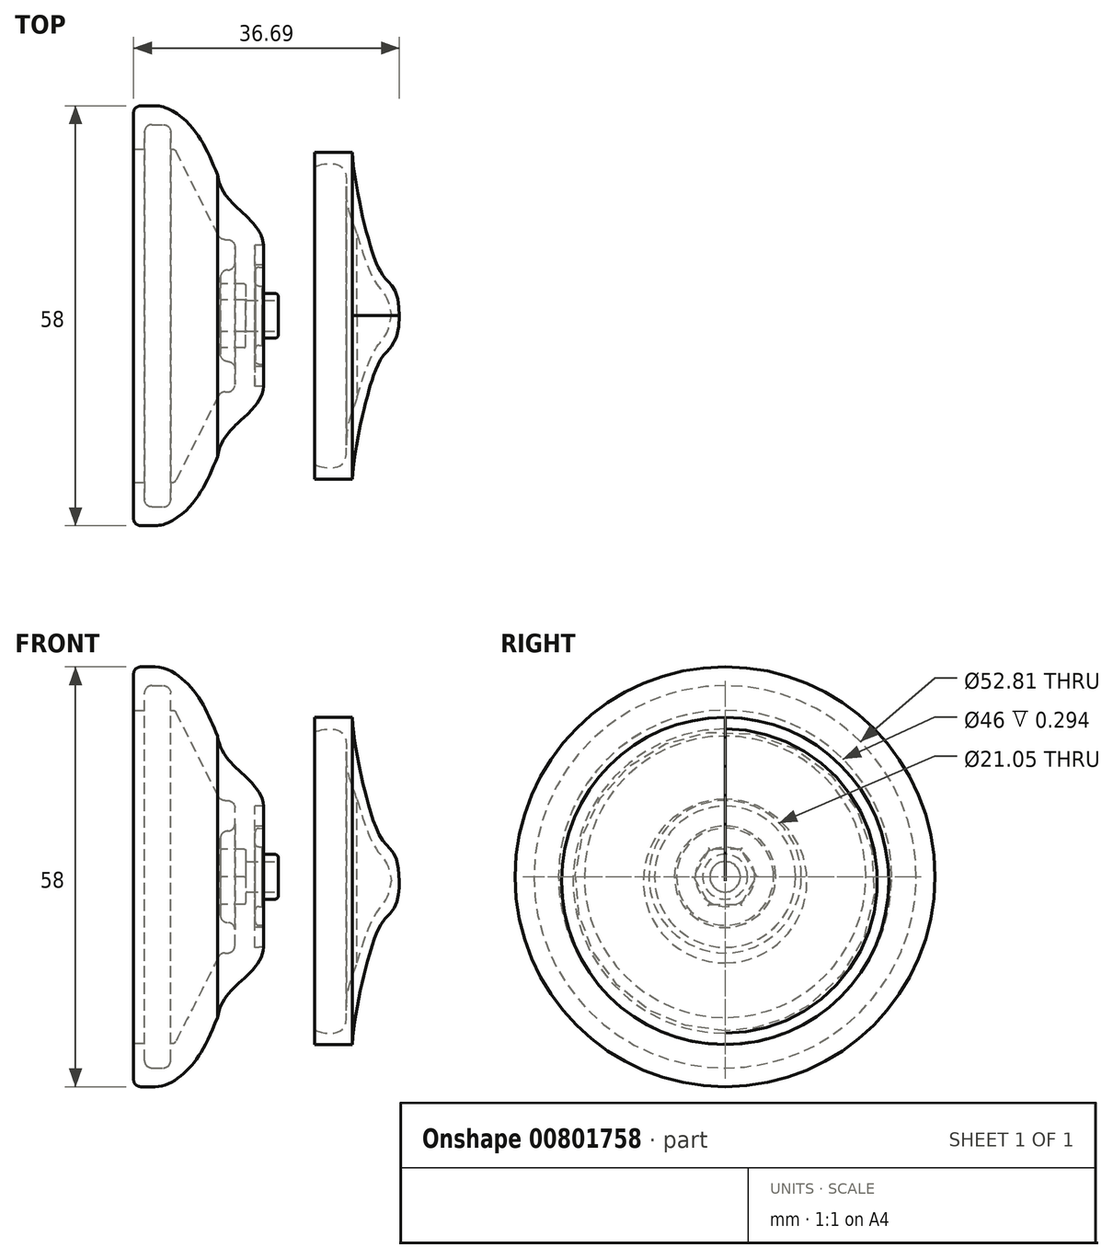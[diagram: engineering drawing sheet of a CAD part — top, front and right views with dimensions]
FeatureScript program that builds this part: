
annotation { "Feature Type Name" : "Feature", "Feature Type Description" : "" }
export const myFeature = defineFeature(function(context is Context, id is Id, definition is map)
    precondition{}
    {
        {
            var Q0;
            Q0=qCreatedBy(makeId("Front.planeOp"),FACE);
            var sketch = newSketch(context, id + "F0", { "sketchPlane" : qUnion([Q0])});
            skPoint(sketch, "E0", {"position": v(36.58, 0) * mm});
            skLineSegment(sketch, "E1", {"start": v(40.53, -3.33) * mm, "end": v(40.53, -2.83) * mm});
            skLineSegment(sketch, "E2", {"start": v(40.03, -2.33) * mm, "end": v(38.28, -2.33) * mm});
            skLineSegment(sketch, "E3", {"start": v(38.28, -2.33) * mm, "end": v(38.28, -1.33) * mm});
            skLineSegment(sketch, "E4", {"start": v(38.28, -1.33) * mm, "end": v(37.83, -1.33) * mm});
            skLineSegment(sketch, "E5", {"start": v(37.33, -0.83) * mm, "end": v(37.33, 0.76) * mm});
            skLineSegment(sketch, "E6", {"start": v(37.82, 1.26) * mm, "end": v(38.46, 1.27) * mm});
            skLineSegment(sketch, "E7", {"start": v(38.46, 1.27) * mm, "end": v(38.46, 1.57) * mm});
            skLineSegment(sketch, "E8", {"start": v(38.46, 1.57) * mm, "end": v(37.26, 1.57) * mm});
            skLineSegment(sketch, "E9", {"start": v(37.26, 1.57) * mm, "end": v(37.26, 4.32) * mm});
            skLineSegment(sketch, "E10", {"start": v(37.26, 4.32) * mm, "end": v(38.46, 4.32) * mm});
            skPoint(sketch, "E11.startSnap0", {"position": v(39.4, -2.33) * mm});
            skLineSegment(sketch, "E12", {"start": v(36.03, -3.33) * mm, "end": v(40.53, -3.33) * mm});
            skLineSegment(sketch, "E13", {"start": v(40.53, -5.43) * mm, "end": v(38.22, -5.43) * mm});
            skLineSegment(sketch, "E14", {"start": v(40.53, -5.43) * mm, "end": v(20.53, -5.43) * mm});
            skLineSegment(sketch, "E15", {"start": v(21.52, 23.57) * mm, "end": v(23.51, 23.57) * mm});
            skFitSpline(sketch, "E16", {"points": [v(23.51, 23.57) * mm, v(27.76, 21.46) * mm, v(32.12, 14) * mm], "startDerivative": vector(10.57, 0) * mm, "endDerivative": vector(7.95, -20.2) * mm});
            skFitSpline(sketch, "E17", {"points": [v(32.12, 14) * mm, v(35.32, 9.04) * mm, v(38.46, 4.32) * mm], "startDerivative": vector(2.45, -14.07) * mm, "endDerivative": vector(0, -11.08) * mm});
            skLineSegment(sketch, "E18", {"start": v(32.53, -0.79) * mm, "end": v(32.53, -3.33) * mm});
            skLineSegment(sketch, "E19", {"start": v(20.53, 22.57) * mm, "end": v(20.54, 17.57) * mm});
            skLineSegment(sketch, "E20", {"start": v(20.54, 17.57) * mm, "end": v(22.04, 17.57) * mm});
            skLineSegment(sketch, "E21", {"start": v(22.04, 17.57) * mm, "end": v(22.04, 19.97) * mm});
            skLineSegment(sketch, "E22", {"start": v(23.04, 20.97) * mm, "end": v(24.64, 20.97) * mm});
            skLineSegment(sketch, "E23", {"start": v(25.64, 19.97) * mm, "end": v(25.64, 17.57) * mm});
            skPoint(sketch, "E24.visualSharp", {"position": v(22.04, 20.97) * mm});
            skArc(sketch, "E24.filletArc", {"start": v(23.04, 20.97) * mm, "mid": v(22.34, 20.68) * mm, "end": v(22.04, 19.97) * mm});
            skPoint(sketch, "E25.visualSharp", {"position": v(25.64, 20.97) * mm});
            skArc(sketch, "E25.filletArc", {"start": v(25.64, 19.97) * mm, "mid": v(25.35, 20.68) * mm, "end": v(24.64, 20.97) * mm});
            skArc(sketch, "E26.filletArc", {"start": v(21.52, 23.57) * mm, "mid": v(20.82, 23.28) * mm, "end": v(20.53, 22.57) * mm});
            skLineSegment(sketch, "E27", {"start": v(25.64, 17.57) * mm, "end": v(25.94, 17.57) * mm});
            skLineSegment(sketch, "E28", {"start": v(26.38, 17.3) * mm, "end": v(32.25, 5.64) * mm});
            skLineSegment(sketch, "E29", {"start": v(33.14, 5.1) * mm, "end": v(33.53, 5.1) * mm});
            skLineSegment(sketch, "E30", {"start": v(34.53, 4.1) * mm, "end": v(34.53, 1.89) * mm});
            skLineSegment(sketch, "E31", {"start": v(33.53, 0.89) * mm, "end": v(33.53, 0.89) * mm});
            skLineSegment(sketch, "E32", {"start": v(32.53, -0.11) * mm, "end": v(32.53, -0.59) * mm});
            skPoint(sketch, "E33.visualSharp", {"position": v(32.53, 5.1) * mm});
            skArc(sketch, "E33.filletArc", {"start": v(32.25, 5.64) * mm, "mid": v(32.62, 5.24) * mm, "end": v(33.14, 5.1) * mm});
            skPoint(sketch, "E34.visualSharp", {"position": v(34.53, 5.1) * mm});
            skArc(sketch, "E34.filletArc", {"start": v(34.53, 4.1) * mm, "mid": v(34.24, 4.8) * mm, "end": v(33.53, 5.1) * mm});
            skPoint(sketch, "E35.visualSharp", {"position": v(34.53, 0.89) * mm});
            skArc(sketch, "E35.filletArc", {"start": v(33.53, 0.89) * mm, "mid": v(34.24, 1.18) * mm, "end": v(34.53, 1.89) * mm});
            skPoint(sketch, "E36.visualSharp", {"position": v(32.53, 0.89) * mm});
            skArc(sketch, "E36.filletArc", {"start": v(33.53, 0.89) * mm, "mid": v(32.82, 0.6) * mm, "end": v(32.53, -0.11) * mm});
            skPoint(sketch, "E37.visualSharp", {"position": v(32.53, -0.79) * mm});
            skPoint(sketch, "E38.visualSharp", {"position": v(35.53, -3.33) * mm});
            skPoint(sketch, "E39.visualSharp", {"position": v(37.33, -1.33) * mm});
            skArc(sketch, "E39.filletArc", {"start": v(37.33, -0.83) * mm, "mid": v(37.48, -1.18) * mm, "end": v(37.83, -1.33) * mm});
            skArc(sketch, "E40.filletArc", {"start": v(37.82, 1.26) * mm, "mid": v(37.47, 1.12) * mm, "end": v(37.33, 0.76) * mm});
            skPoint(sketch, "E41.visualSharp", {"position": v(40.53, -2.33) * mm});
            skArc(sketch, "E41.filletArc", {"start": v(40.53, -2.83) * mm, "mid": v(40.38, -2.48) * mm, "end": v(40.03, -2.33) * mm});
            skPoint(sketch, "E42.visualSharp", {"position": v(26.24, 17.57) * mm});
            skArc(sketch, "E42.filletArc", {"start": v(26.38, 17.3) * mm, "mid": v(26.2, 17.5) * mm, "end": v(25.94, 17.57) * mm});
            skLineSegment(sketch, "E43", {"start": v(36.03, -3.33) * mm, "end": v(32.53, -3.33) * mm});
            skLineSegment(sketch, "E44", {"start": v(32.53, -0.59) * mm, "end": v(32.53, -0.79) * mm});
            skPoint(sketch, "E45.orphan", {"position": v(32.53, -5.43) * mm});
            skSolve(sketch);
        }
        {
            var Q0;
            Q0=qCreatedBy(makeId("Front.planeOp"),FACE);
            var sketch = newSketch(context, id + "F1", { "sketchPlane" : qUnion([Q0])});
            skLineSegment(sketch, "E46", {"start": v(45.52, -6.03) * mm, "end": v(45.52, 16.57) * mm});
            skLineSegment(sketch, "E47", {"start": v(45.52, 16.57) * mm, "end": v(57.22, 16.57) * mm});
            skLineSegment(sketch, "E48", {"start": v(57.22, 16.57) * mm, "end": v(57.22, -6.03) * mm});
            skLineSegment(sketch, "E49", {"start": v(57.22, -6.03) * mm, "end": v(45.52, -6.03) * mm});
            skLineSegment(sketch, "E50", {"start": v(45.52, 16.57) * mm, "end": v(50.72, 16.57) * mm});
            skLineSegment(sketch, "E51", {"start": v(45.52, 16.57) * mm, "end": v(45.52, 14.57) * mm});
            skPoint(sketch, "E52.1.internal.snap0", {"position": v(48.12, 16.57) * mm});
            skFitSpline(sketch, "E53", {"points": [v(45.52, 14.57) * mm, v(49.42, 14.37) * mm, v(49.98, 10.23) * mm, v(51.39, 5.27) * mm], "startDerivative": vector(14.16, 5.38) * mm, "endDerivative": vector(5.05, -15.1) * mm});
            skFitSpline(sketch, "E54", {"points": [v(51.39, 5.27) * mm, v(53.79, -1.19) * mm, v(55.5, -3.64) * mm, v(56.14, -6.03) * mm], "startDerivative": vector(3.62, -12.47) * mm, "endDerivative": vector(1.6, -7.9) * mm});
            skFitSpline(sketch, "E55", {"points": [v(50.72, 16.57) * mm, v(51.63, 10.15) * mm, v(52.8, 5.16) * mm, v(55.04, -0.56) * mm, v(57.22, -6.03) * mm], "startDerivative": vector(1.32, -24.15) * mm, "endDerivative": vector(0, -48.08) * mm});
            skSolve(sketch);
        }
        {
            var Q0;
            {var subQ0=sQuery(id+"F1.wireOp",EDGE,"E53");Q0=makeQuery(id+"F1.imprint","IMPRINT",FACE,{"disambiguationData":[TD([[makeQuery(id+"F1.imprint","IMPRINT",EDGE,{"derivedFrom":subQ0}),1.0]])]});}
            var Q1;
            Q1=sQuery(id+"F1.wireOp",EDGE,"E49");
            revolve(context, id + "F2", {"surfaceOperationType" : NewSurfaceOperationType.NEW, "entities" : qUnion([Q0]), "axis" : qUnion([Q1]), "revolveType" : RevolveType.FULL});
        }
        {
            var Q0;
            Q0 = qSketchRegion(id + "F0", true);
            var Q1;
            Q1=sQuery(id+"F0.wireOp",EDGE,"E14");
            revolve(context, id + "F3", {"surfaceOperationType" : NewSurfaceOperationType.NEW, "entities" : qUnion([Q0]), "axis" : qUnion([Q1]), "revolveType" : RevolveType.FULL});
        }
        {
            var Q0;
            Q0=makeQuery(id+"F3.opRevolve","SWEPT_FACE",FACE,{"disambiguationData":[OSD([sQuery(id+"F0.wireOp",EDGE,"E18"),sQuery(id+"F0.wireOp",EDGE,"E32"),sQuery(id+"F0.wireOp",EDGE,"E44")])]});
            var sketch = newSketch(context, id + "F4", { "sketchPlane" : qUnion([Q0])});
            skPoint(sketch, "E56.0.midPoint", {"position": v(0, -1.31) * mm});
            skLineSegment(sketch, "E57.0", {"start": v(2.2, -9.21) * mm, "end": v(-2.2, -9.21) * mm});
            skLineSegment(sketch, "E57.1", {"start": v(-2.2, -9.21) * mm, "end": v(-4.39, -5.41) * mm});
            skLineSegment(sketch, "E57.2", {"start": v(-4.39, -5.41) * mm, "end": v(-2.2, -1.61) * mm});
            skLineSegment(sketch, "E57.3", {"start": v(-2.2, -1.61) * mm, "end": v(2.2, -1.61) * mm});
            skLineSegment(sketch, "E57.4", {"start": v(2.2, -1.61) * mm, "end": v(4.39, -5.41) * mm});
            skLineSegment(sketch, "E57.5", {"start": v(4.39, -5.41) * mm, "end": v(2.2, -9.21) * mm});
            skPoint(sketch, "E57.0.midPoint", {"position": v(0, -9.21) * mm});
            skSolve(sketch);
        }
        {
            var Q0;
            Q0=makeQuery(id+"F4.imprint","IMPRINT",FACE,{"disambiguationData":[TD([[makeQuery(id+"F4.imprint","IMPRINT",EDGE,{"derivedFrom":sQuery(id+"F4.wireOp",EDGE,"E57.0")}),-1.0]])]});
            extrude(context, id + "F5", {"entities" : qUnion([Q0]), "operationType" : NewBodyOperationType.REMOVE, "oppositeDirection" : true, "depth" : 3.5 * mm, "offsetDistance" : 25 * mm});
        }
        {
            var Q0;
            Q0=makeQuery(id+"F5.boolean.opBoolean","COPY",FACE,{"derivedFrom":makeQuery(id+"F5.opExtrude","CAP_FACE",FACE,{"disambiguationData":[OSD([sQuery(id+"F0.wireOp",EDGE,"E18"),sQuery(id+"F0.wireOp",EDGE,"E43"),sQuery(id+"F4.wireOp",EDGE,"E56.0"),sQuery(id+"F4.wireOp",EDGE,"E56.1"),sQuery(id+"F4.wireOp",EDGE,"E56.2"),sQuery(id+"F4.wireOp",EDGE,"E56.3"),sQuery(id+"F4.wireOp",EDGE,"E56.4"),sQuery(id+"F4.wireOp",EDGE,"E56.5")])],"isStart":false})});
            fillet(context, id + "F6", {"entities" : qUnion([Q0]), "radius" : .2 * mm, "tangentPropagation" : true, "allowEdgeOverflow" : false});
        }
        {
            var Q0;
            Q0=makeQuery(id+"F3.opRevolve","SWEPT_FACE",FACE,{"disambiguationData":[OSD([sQuery(id+"F0.wireOp",EDGE,"E18"),sQuery(id+"F0.wireOp",EDGE,"E32"),sQuery(id+"F0.wireOp",EDGE,"E44")])]});
            fillet(context, id + "F7", {"entities" : qUnion([Q0]), "radius" : .2 * mm, "tangentPropagation" : true, "allowEdgeOverflow" : false});
        }
        {
            var Q0;
            Q0=makeQuery(id+"F2.opRevolve","SWEPT_EDGE",EDGE,{"disambiguationData":[OSD([sQuery(id+"F1.wireOp",EDGE,"E46"),sQuery(id+"F1.wireOp",EDGE,"E53")])]});
            fillet(context, id + "F8", {"entities" : qUnion([Q0]), "radius" : .2 * mm, "tangentPropagation" : true, "allowEdgeOverflow" : false});
        }
    });
